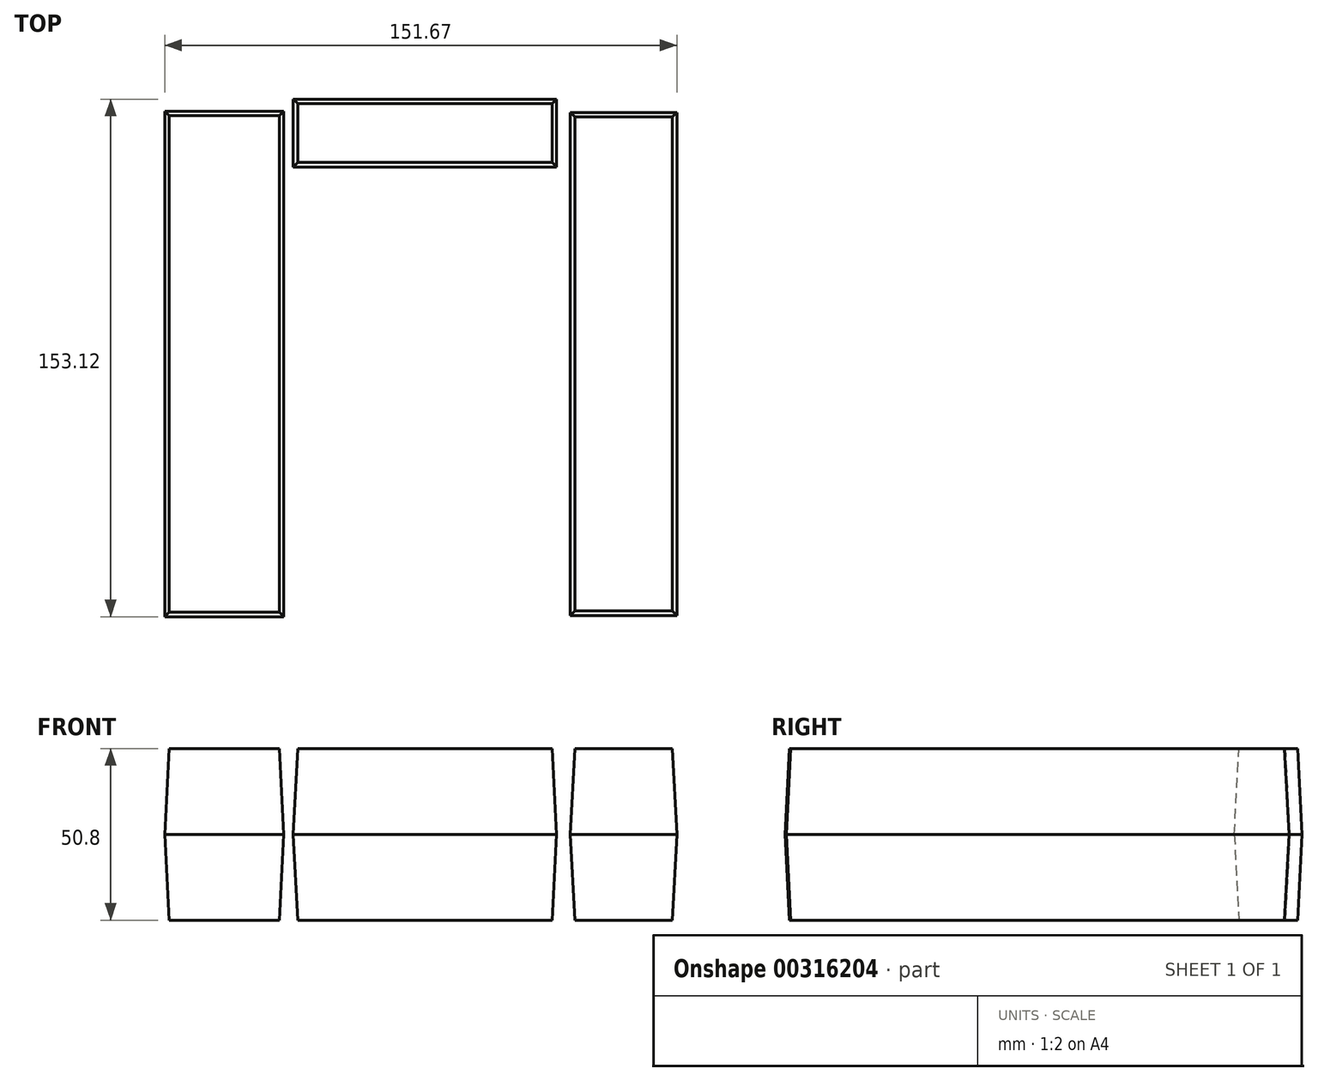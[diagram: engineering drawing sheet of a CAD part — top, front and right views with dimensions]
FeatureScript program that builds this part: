
annotation { "Feature Type Name" : "Feature", "Feature Type Description" : "" }
export const myFeature = defineFeature(function(context is Context, id is Id, definition is map)
    precondition{}
    {
        {
            var Q0;
            Q0=qCreatedBy(makeId("Top.planeOp"),FACE);
            var sketch = newSketch(context, id + "F0", { "sketchPlane" : qUnion([Q0])});
            skLineSegment(sketch, "E0.bottom", {"start": v(-75.6, -74.87) * mm, "end": v(-40.32, -74.87) * mm});
            skLineSegment(sketch, "E0.top", {"start": v(-75.6, 74.68) * mm, "end": v(-40.32, 74.68) * mm});
            skLineSegment(sketch, "E0.left", {"start": v(-75.6, -74.87) * mm, "end": v(-75.6, 74.68) * mm});
            skLineSegment(sketch, "E0.right", {"start": v(-40.32, -74.87) * mm, "end": v(-40.32, 74.68) * mm});
            skSolve(sketch);
        }
        {
            var Q0;
            Q0 = qSketchRegion(id + "F0", true);
            extrude(context, id + "F1", {"entities" : qUnion([Q0]), "oppositeDirection" : true, "depth" : 25.4 * mm, "hasDraft" : true, "draftAngle" : 3 * degree, "draftPullDirection" : true, "hasSecondDirection" : true, "secondDirectionOppositeDirection" : false, "secondDirectionDepth" : 25.4 * mm, "hasSecondDirectionDraft" : true, "secondDirectionDraftAngle" : 3 * degree, "secondDirectionDraftPullDirection" : true});
        }
        {
            var Q0;
            Q0=qCreatedBy(makeId("Top.planeOp"),FACE);
            var sketch = newSketch(context, id + "F2", { "sketchPlane" : qUnion([Q0])});
            skLineSegment(sketch, "E1.bottom", {"start": v(76.07, -74.5) * mm, "end": v(44.48, -74.5) * mm});
            skLineSegment(sketch, "E1.top", {"start": v(76.07, 74.32) * mm, "end": v(44.48, 74.32) * mm});
            skLineSegment(sketch, "E1.left", {"start": v(76.07, -74.5) * mm, "end": v(76.07, 74.32) * mm});
            skLineSegment(sketch, "E1.right", {"start": v(44.48, -74.5) * mm, "end": v(44.48, 74.32) * mm});
            skSolve(sketch);
        }
        {
            var Q0;
            Q0=makeQuery(id+"F2.imprint","IMPRINT",FACE,{"disambiguationData":[TD([[makeQuery(id+"F2.imprint","IMPRINT",EDGE,{"derivedFrom":sQuery(id+"F2.wireOp",EDGE,"E1.bottom")}),-1.0]])]});
            extrude(context, id + "F3", {"entities" : qUnion([Q0]), "depth" : 25.4 * mm, "hasDraft" : true, "draftAngle" : 3 * degree, "draftPullDirection" : true, "hasSecondDirection" : true, "secondDirectionOppositeDirection" : true, "secondDirectionDepth" : 25.4 * mm, "hasSecondDirectionDraft" : true, "secondDirectionDraftAngle" : 3 * degree, "secondDirectionDraftPullDirection" : true});
        }
        {
            var Q0;
            Q0=qCreatedBy(makeId("Top.planeOp"),FACE);
            var sketch = newSketch(context, id + "F4", { "sketchPlane" : qUnion([Q0])});
            skLineSegment(sketch, "E2.bottom", {"start": v(-37.53, 78.25) * mm, "end": v(40.46, 78.25) * mm});
            skLineSegment(sketch, "E2.top", {"start": v(-37.53, 58.17) * mm, "end": v(40.46, 58.17) * mm});
            skLineSegment(sketch, "E2.left", {"start": v(-37.53, 78.25) * mm, "end": v(-37.53, 58.17) * mm});
            skLineSegment(sketch, "E2.right", {"start": v(40.46, 78.25) * mm, "end": v(40.46, 58.17) * mm});
            skSolve(sketch);
        }
        {
            var Q0;
            Q0 = qSketchRegion(id + "F4", true);
            extrude(context, id + "F5", {"entities" : qUnion([Q0]), "oppositeDirection" : true, "depth" : 25.4 * mm, "hasDraft" : true, "draftAngle" : 3 * degree, "draftPullDirection" : true, "hasSecondDirection" : true, "secondDirectionOppositeDirection" : false, "secondDirectionDepth" : 25.4 * mm, "hasSecondDirectionDraft" : true, "secondDirectionDraftAngle" : 3 * degree, "secondDirectionDraftPullDirection" : true});
        }
    });
